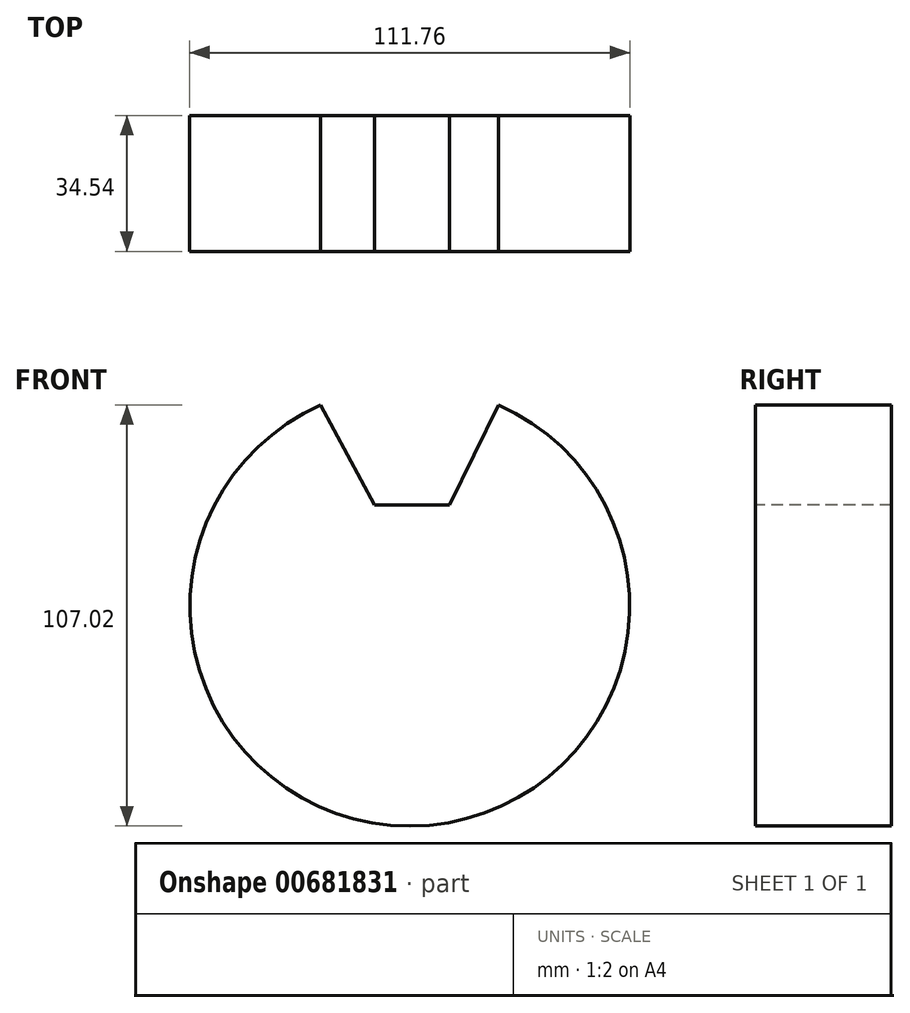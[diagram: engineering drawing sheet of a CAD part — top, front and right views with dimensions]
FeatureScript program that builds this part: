
annotation { "Feature Type Name" : "Feature", "Feature Type Description" : "" }
export const myFeature = defineFeature(function(context is Context, id is Id, definition is map)
    precondition{}
    {
        {
            var Q0;
            Q0=qCreatedBy(makeId("Front.planeOp"),FACE);
            var sketch = newSketch(context, id + "F0", { "sketchPlane" : qUnion([Q0])});
            skCircle(sketch, "E0", {"center": v(0.08, -31.74) * mm, "radius": 55.88 * mm});
            skLineSegment(sketch, "E1", {"start": v(-22.56, 19.35) * mm, "end": v(-8.86, -6) * mm});
            skLineSegment(sketch, "E2", {"start": v(-8.86, -6) * mm, "end": v(10.2, -6) * mm});
            skLineSegment(sketch, "E3", {"start": v(10.2, -6) * mm, "end": v(22.6, 19.4) * mm});
            skSolve(sketch);
        }
        {
            var Q0;
            Q0=makeQuery(id+"F0.imprint","IMPRINT",FACE,{"disambiguationData":[TD([[makeQuery(id+"F0.imprint","IMPRINT",EDGE,{"derivedFrom":sQuery(id+"F0.wireOp",EDGE,"NtdytaIU-CAuz-7bdZ-M3LZ-XDD6lqNfVwvr.bottom")}),1.0]])]});
            var Q1;
            Q1=makeQuery(id+"F0.imprint","IMPRINT",FACE,{"disambiguationData":[TD([[makeQuery(id+"F0.imprint","IMPRINT",EDGE,{"derivedFrom":sQuery(id+"F0.wireOp",EDGE,"NtdytaIU-CAuz-7bdZ-M3LZ-XDD6lqNfVwvr.bottom")}),-1.0]])]});
            var Q2;
            {var subQ0=sQuery(id+"F0.wireOp",EDGE,"NtdytaIU-CAuz-7bdZ-M3LZ-XDD6lqNfVwvr.top");var subQ1=sQuery(id+"F0.wireOp",EDGE,"axLVT8E8-mtLE-t4VZ-Noz4-n5sBeJWqdxxC");var subQ2=makeQuery(id+"F0.imprint","INTERSECT",VERTEX,{"disambiguationData":[OD(0.0)],"derivedFrom":[subQ1,subQ0]});Q2=makeQuery(id+"F0.imprint","IMPRINT",FACE,{"disambiguationData":[TD([[makeQuery(id+"F0.imprint","IMPRINT",EDGE,{"disambiguationData":[TD([[subQ2,1.0]])],"derivedFrom":subQ1}),1.0]])]});}
            var Q3;
            Q3=makeQuery(id+"F0.imprint","IMPRINT",FACE,{"disambiguationData":[TD([[makeQuery(id+"F0.imprint","IMPRINT",EDGE,{"derivedFrom":sQuery(id+"F0.wireOp",EDGE,"axLVT8E8-mtLE-t4VZ-Noz4-n5sBeJWqdxxC")}),-1.0]])]});
            var Q4;
            Q4=makeQuery(id+"F0.imprint","IMPRINT",FACE,{"disambiguationData":[TD([[makeQuery(id+"F0.imprint","IMPRINT",EDGE,{"derivedFrom":sQuery(id+"F0.wireOp",EDGE,"axLVT8E8-mtLE-t4VZ-Noz4-n5sBeJWqdxxC")}),1.0]])]});
            var Q5;
            {var subQ0=sQuery(id+"F0.wireOp",EDGE,"E1");Q5=makeQuery(id+"F0.imprint","IMPRINT",FACE,{"disambiguationData":[TD([[makeQuery(id+"F0.imprint","IMPRINT",EDGE,{"derivedFrom":subQ0}),-1.0]])]});}
            extrude(context, id + "F1", {"entities" : qUnion([Q0, Q1, Q2, Q3, Q4, Q5]), "oppositeDirection" : true, "depth" : 34.54 * mm, "offsetDistance" : 25.4 * mm});
        }
    });
